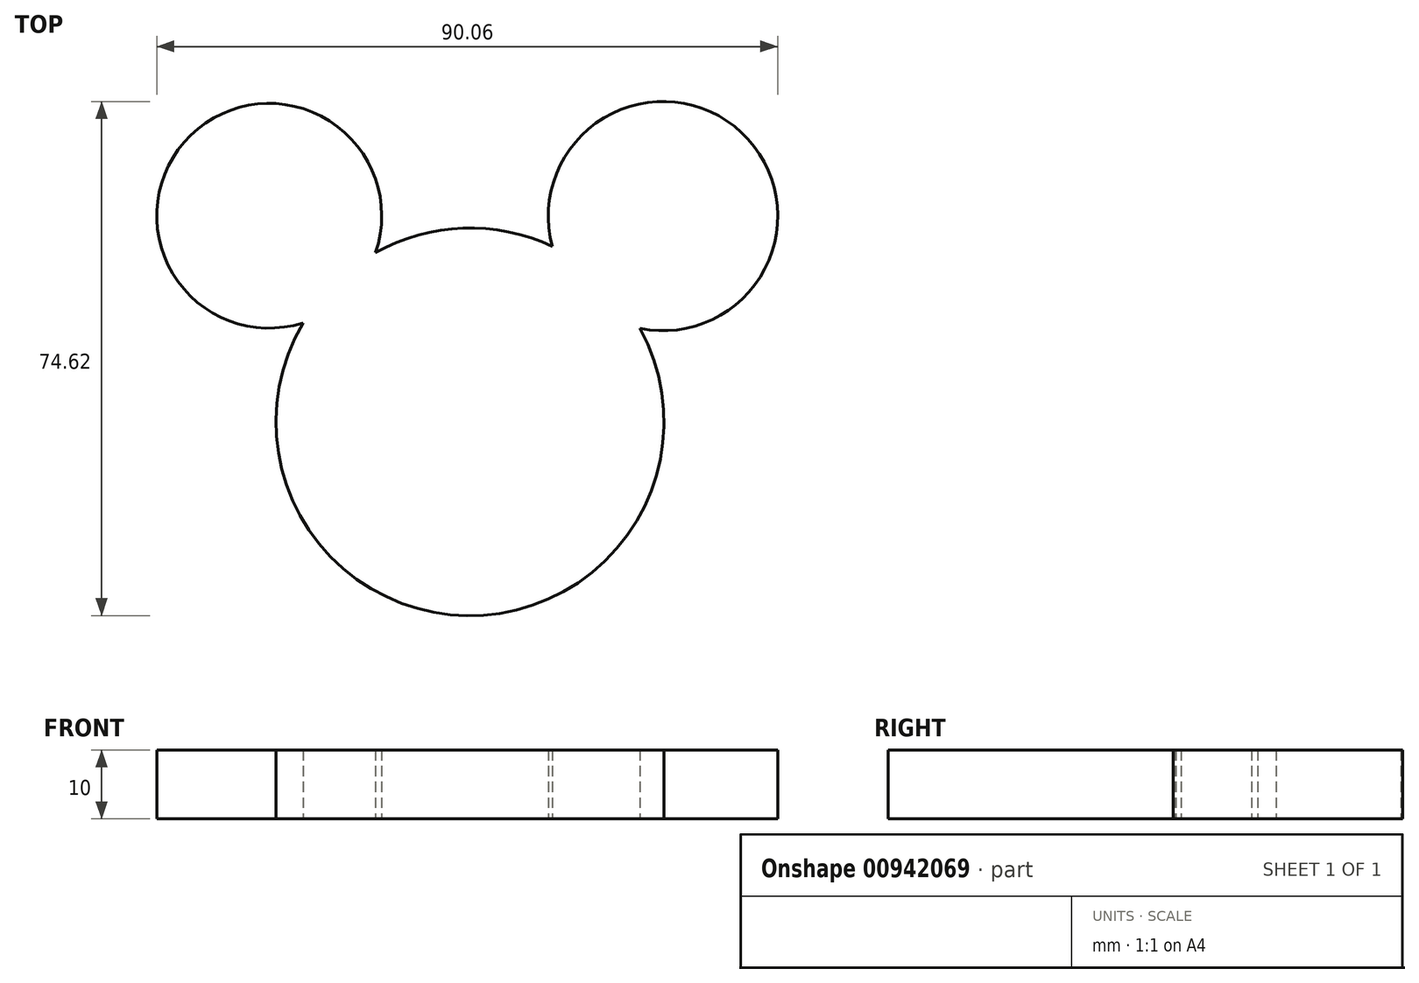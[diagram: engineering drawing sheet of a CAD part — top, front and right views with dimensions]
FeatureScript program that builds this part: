
annotation { "Feature Type Name" : "Feature", "Feature Type Description" : "" }
export const myFeature = defineFeature(function(context is Context, id is Id, definition is map)
    precondition{}
    {
        {
            var Q0;
            Q0=qCreatedBy(makeId("Top.planeOp"),FACE);
            var sketch = newSketch(context, id + "F0", { "sketchPlane" : qUnion([Q0])});
            skCircle(sketch, "E0", {"center": v(-6.1, -8.42) * mm, "radius": 28.13 * mm});
            skPoint(sketch, "E0.first.point", {"position": v(-5.99, 19.71) * mm});
            skPoint(sketch, "E0.second.point", {"position": v(-2.77, -36.35) * mm});
            skPoint(sketch, "E0.third.point", {"position": v(-22.34, -31.4) * mm});
            skCircle(sketch, "E1", {"center": v(-35.2, 21.48) * mm, "radius": 16.31 * mm});
            skPoint(sketch, "E1.first.point", {"position": v(-46.87, 10.07) * mm});
            skPoint(sketch, "E1.second.point", {"position": v(-47.45, 32.27) * mm});
            skPoint(sketch, "E1.third.point", {"position": v(-23.8, 33.14) * mm});
            skCircle(sketch, "E2", {"center": v(21.9, 21.44) * mm, "radius": 16.64 * mm});
            skPoint(sketch, "E2.first.point", {"position": v(6.57, 27.89) * mm});
            skPoint(sketch, "E2.second.point", {"position": v(33.73, 33.14) * mm});
            skPoint(sketch, "E2.third.point", {"position": v(29.93, 6.86) * mm});
            skSolve(sketch);
        }
        {
            var Q0;
            Q0 = qSketchRegion(id + "F0", true);
            extrude(context, id + "F1", {"entities" : qUnion([Q0]), "depth" : 10 * mm, "offsetDistance" : 25.4 * mm});
        }
    });
